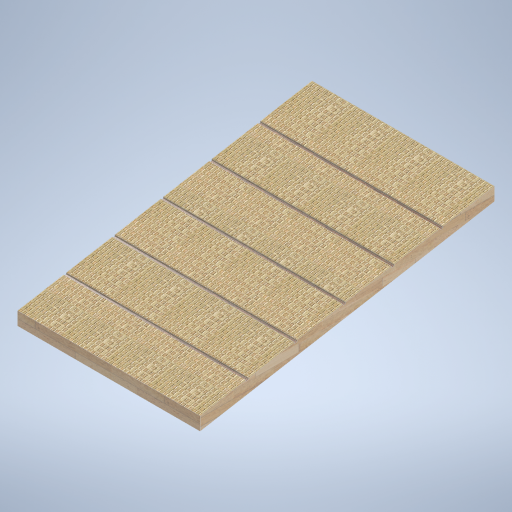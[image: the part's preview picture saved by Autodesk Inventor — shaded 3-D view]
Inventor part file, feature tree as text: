
AUTODESK INVENTOR PART (.ipt)
format: ipt  version: 2024.2 (Build 282272000, 272)  size: 499,200 bytes
history: native  units: mm
features: sketch x5, plane x3, loft x1, extrude x1, projected_geometry x1
ambient origin geometry x8: Origin, YZ Plane, XZ Plane, XY Plane, X Axis, Y Axis, Z Axis, Center Point
bodies: Solid1 (feature_tree)
feature tree (11):
  plane  "Work Plane2"
  sketch  "Sketch1"  dims[d0=0.0mm d1=2209.0mm d2=1369.0mm]
  sketch  "Sketch2"  dims[d3=100.0mm d4=17.453293mm]
  plane  "Work Plane3"
  sketch  "Sketch3"  dims[d5=100.0mm]
  loft  "Loft1"
  extrude  "Extrusion1"  Depth=100.0mm
  plane  "Work Plane1"
  sketch  "Sketch4"  dims[d6=0.0mm d7=90.0deg]
  sketch  "Sketch5"  dims[d8=0.0mm d9=90.0deg d10=350.0mm d11=10.0mm d12=20.0mm d13=350.0mm d14=20.0mm d15=350.0mm d16=350.0mm d17=350.0mm d18=0.0mm d19=0.0mm]
  projected_geometry  "Projected Loop1"
